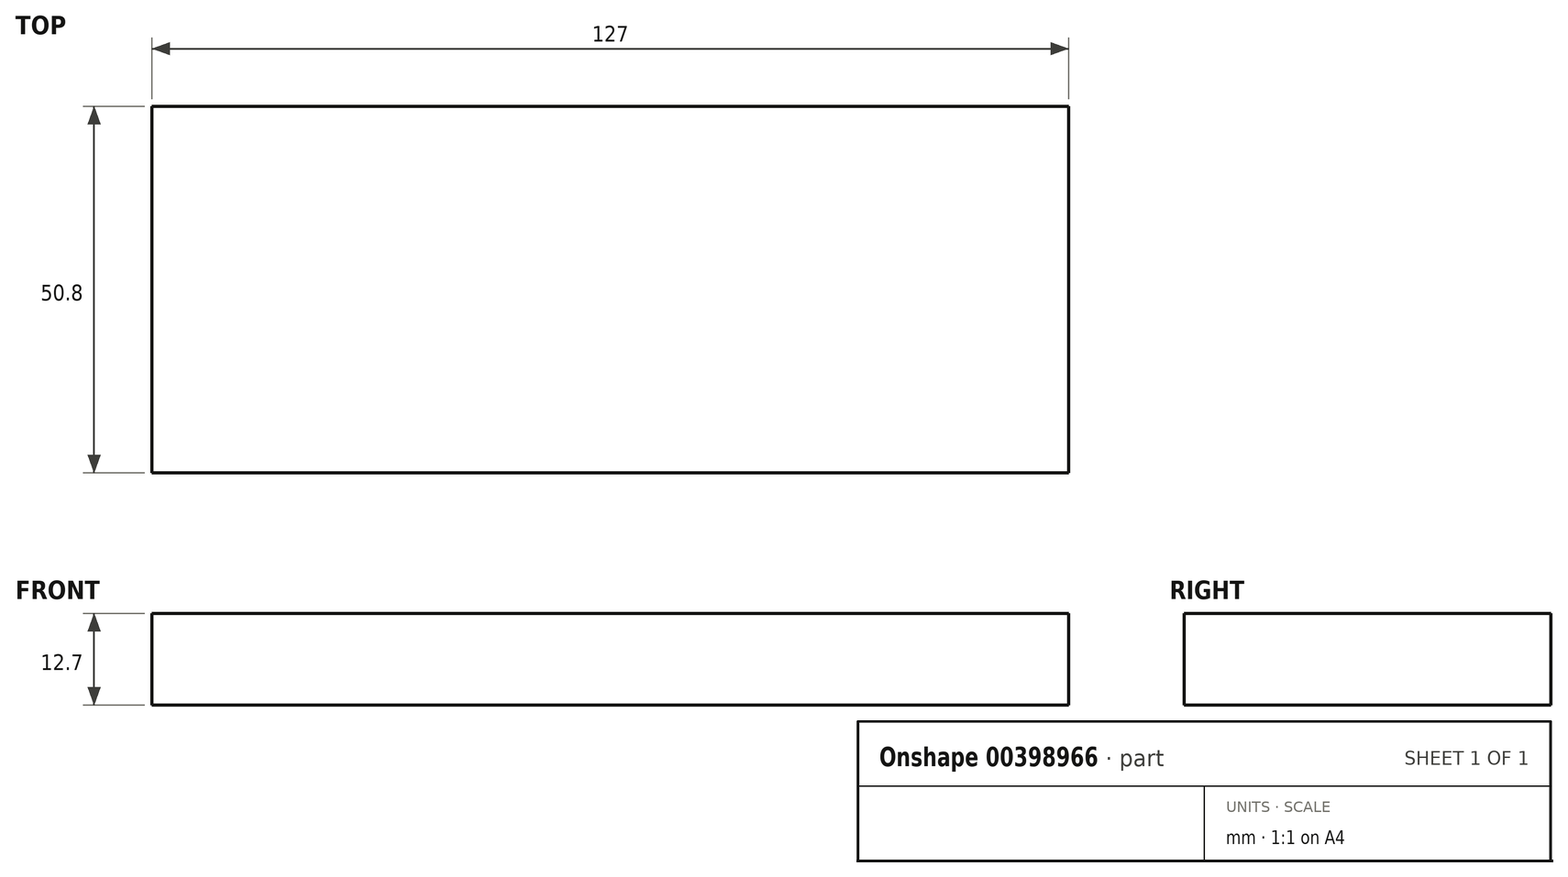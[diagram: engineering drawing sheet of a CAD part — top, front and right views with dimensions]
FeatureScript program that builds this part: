
annotation { "Feature Type Name" : "Feature", "Feature Type Description" : "" }
export const myFeature = defineFeature(function(context is Context, id is Id, definition is map)
    precondition{}
    {
        {
            var Q0;
            Q0=qCreatedBy(makeId("Top.planeOp"),FACE);
            var sketch = newSketch(context, id + "F0", { "sketchPlane" : qUnion([Q0])});
            skLineSegment(sketch, "E0.bottom", {"start": v(63.5, 25.4) * mm, "end": v(-63.5, 25.4) * mm});
            skLineSegment(sketch, "E0.top", {"start": v(63.5, -25.4) * mm, "end": v(-63.5, -25.4) * mm});
            skLineSegment(sketch, "E0.left", {"start": v(63.5, 25.4) * mm, "end": v(63.5, -25.4) * mm});
            skLineSegment(sketch, "E0.right", {"start": v(-63.5, 25.4) * mm, "end": v(-63.5, -25.4) * mm});
            skPoint(sketch, "E0.middle", {"position": v(0, 0) * mm});
            skSolve(sketch);
        }
        {
            var Q0;
            Q0 = qSketchRegion(id + "F0", true);
            extrude(context, id + "F1", {"entities" : qUnion([Q0]), "depth" : 12.7 * mm});
        }
    });
